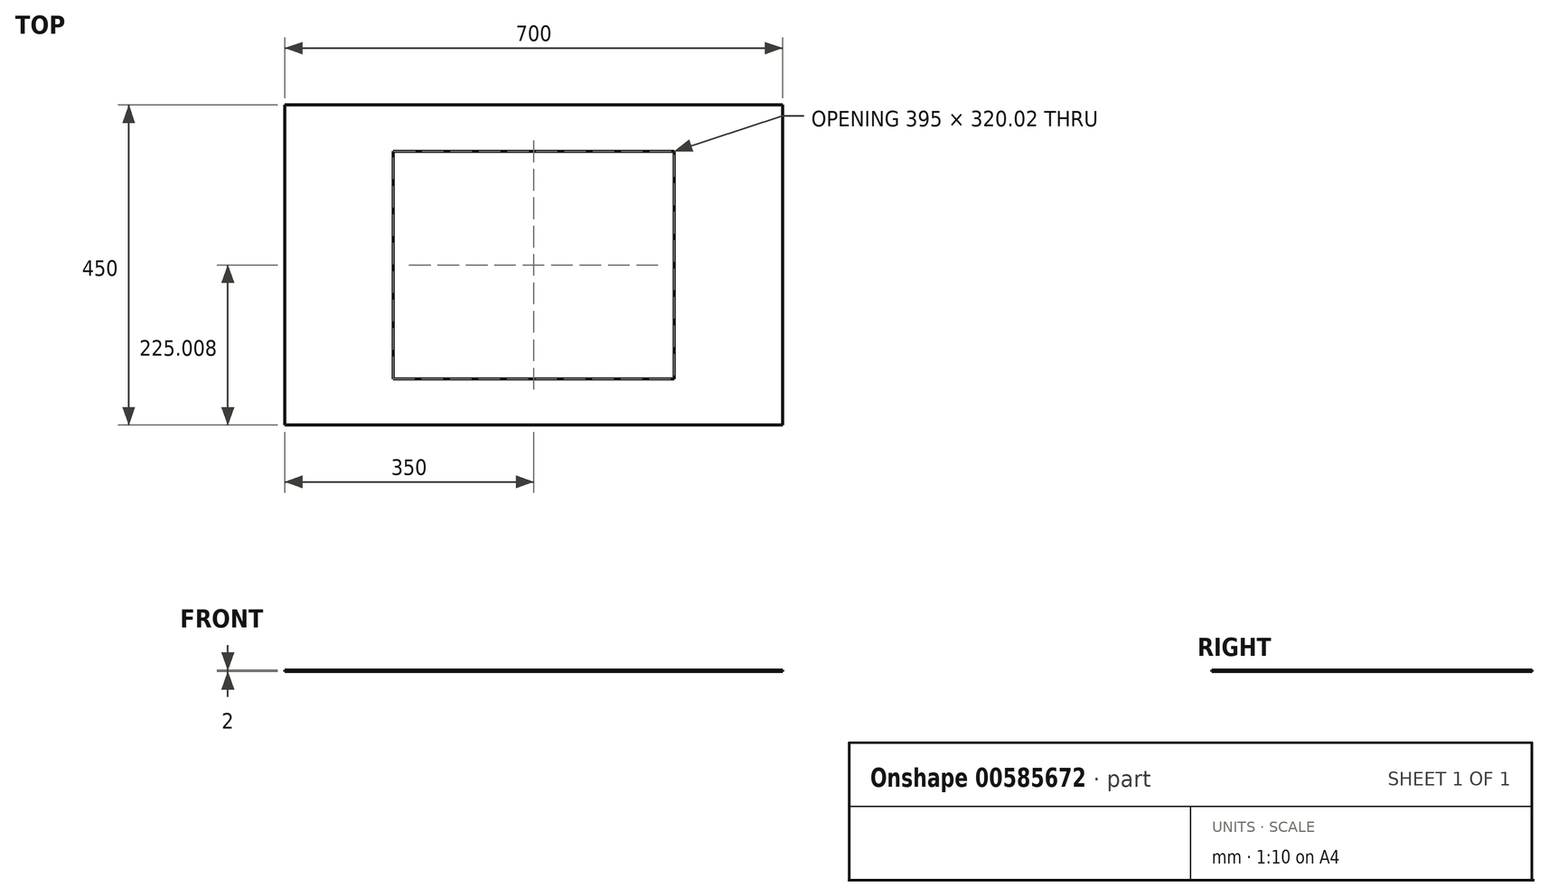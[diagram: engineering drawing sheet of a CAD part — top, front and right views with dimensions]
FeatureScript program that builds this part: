
annotation { "Feature Type Name" : "Feature", "Feature Type Description" : "" }
export const myFeature = defineFeature(function(context is Context, id is Id, definition is map)
    precondition{}
    {
        {
            var Q0;
            Q0=qCreatedBy(makeId("Top.planeOp"),FACE);
            var sketch = newSketch(context, id + "F0", { "sketchPlane" : qUnion([Q0])});
            skLineSegment(sketch, "E0.bottom", {"start": v(350, -225) * mm, "end": v(-350, -225) * mm});
            skLineSegment(sketch, "E0.top", {"start": v(350, 225) * mm, "end": v(-350, 225) * mm});
            skLineSegment(sketch, "E0.left", {"start": v(350, -225) * mm, "end": v(350, 225) * mm});
            skLineSegment(sketch, "E0.right", {"start": v(-350, -225) * mm, "end": v(-350, 225) * mm});
            skPoint(sketch, "E0.middle", {"position": v(0, 0) * mm});
            skLineSegment(sketch, "E1", {"start": v(350, 225) * mm, "end": v(350, -217.25) * mm});
            skLineSegment(sketch, "E2.bottom", {"start": v(197.5, -160) * mm, "end": v(-197.5, -160) * mm});
            skLineSegment(sketch, "E2.top", {"start": v(197.5, 160) * mm, "end": v(-197.5, 160) * mm});
            skLineSegment(sketch, "E2.left", {"start": v(197.5, -160) * mm, "end": v(197.5, 160) * mm});
            skLineSegment(sketch, "E2.right", {"start": v(-197.5, -160) * mm, "end": v(-197.5, 160) * mm});
            skArc(sketch, "E3", {"start": v(-80.7, 160) * mm, "mid": v(-150.6, 139.94) * mm, "end": v(-197.5, 84.37) * mm});
            skPoint(sketch, "E4", {"position": v(-197.5, 0) * mm});
            skSolve(sketch);
        }
        {
            var Q0;
            Q0=sQuery(id+"F0.wireOp",EDGE,"E1");
            extrude(context, id + "F1", {"bodyType" : ToolBodyType.SURFACE, "surfaceEntities" : qUnion([Q0]), "depth" : -40 * mm, "offsetDistance" : 25 * mm});
        }
        {
            var Q0;
            Q0=makeQuery(id+"F0.imprint","IMPRINT",FACE,{"disambiguationData":[TD([[makeQuery(id+"F0.imprint","IMPRINT",EDGE,{"derivedFrom":sQuery(id+"F0.wireOp",EDGE,"E0.bottom")}),-1.0]])]});
            extrude(context, id + "F2", {"entities" : qUnion([Q0]), "depth" : 2 * mm, "offsetDistance" : 25 * mm});
        }
    });
